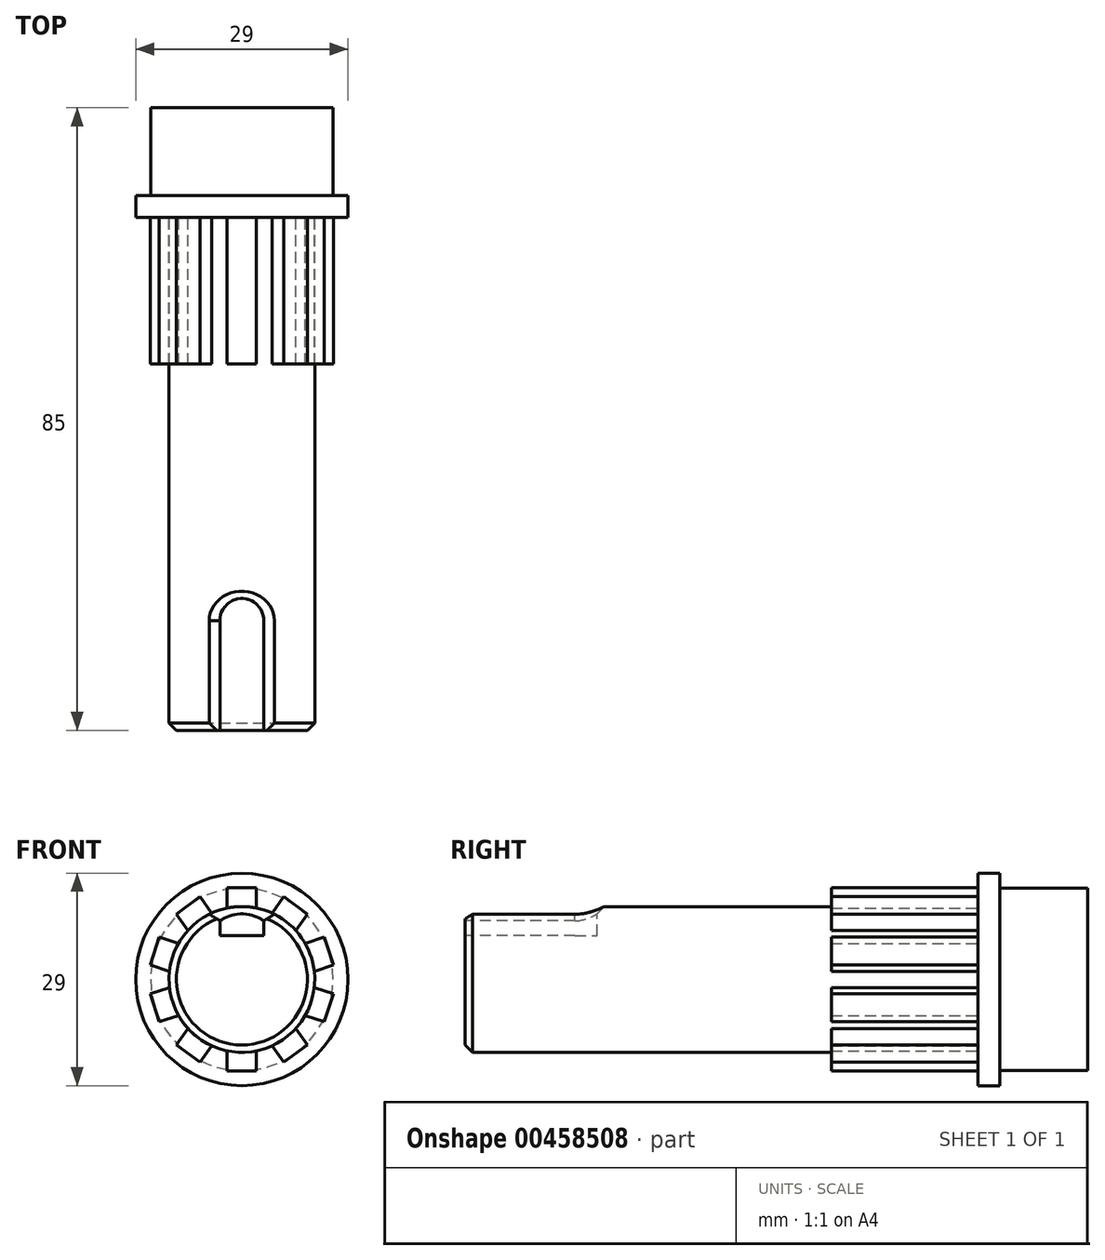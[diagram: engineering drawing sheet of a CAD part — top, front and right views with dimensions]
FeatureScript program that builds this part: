
annotation { "Feature Type Name" : "Feature", "Feature Type Description" : "" }
export const myFeature = defineFeature(function(context is Context, id is Id, definition is map)
    precondition{}
    {
        {
            var Q0;
            Q0=qCreatedBy(makeId("Front.planeOp"),FACE);
            var sketch = newSketch(context, id + "F0", { "sketchPlane" : qUnion([Q0])});
            skCircle(sketch, "E0", {"center": v(0, 0) * mm, "radius": 9.95 * mm});
            skLineSegment(sketch, "E1.bottom", {"start": v(-12.5, 2) * mm, "end": v(12.5, 2) * mm});
            skLineSegment(sketch, "E1.top", {"start": v(-12.5, -2) * mm, "end": v(12.5, -2) * mm});
            skLineSegment(sketch, "E1.left", {"start": v(-12.5, 2) * mm, "end": v(-12.5, -2) * mm});
            skLineSegment(sketch, "E1.right", {"start": v(12.5, 2) * mm, "end": v(12.5, -2) * mm});
            skSolve(sketch);
        }
        {
            var Q0;
            {var subQ0=sQuery(id+"F0.wireOp",EDGE,"E1.bottom");var subQ1=sQuery(id+"F0.wireOp",EDGE,"E0");var subQ2=makeQuery(id+"F0.imprint","INTERSECT",VERTEX,{"disambiguationData":[OD(0.0)],"derivedFrom":[subQ1,subQ0]});Q0=makeQuery(id+"F0.imprint","IMPRINT",FACE,{"disambiguationData":[TD([[makeQuery(id+"F0.imprint","IMPRINT",EDGE,{"disambiguationData":[TD([[subQ2,1.0]])],"derivedFrom":subQ1}),1.0]])]});}
            var Q1;
            {var subQ0=sQuery(id+"F0.wireOp",EDGE,"E1.top");var subQ1=sQuery(id+"F0.wireOp",EDGE,"E0");var subQ2=makeQuery(id+"F0.imprint","INTERSECT",VERTEX,{"disambiguationData":[OD(0.0)],"derivedFrom":[subQ1,subQ0]});Q1=makeQuery(id+"F0.imprint","IMPRINT",FACE,{"disambiguationData":[TD([[makeQuery(id+"F0.imprint","IMPRINT",EDGE,{"disambiguationData":[TD([[subQ2,-1.0]])],"derivedFrom":subQ1}),1.0]])]});}
            var Q2;
            {var subQ5=sQuery(id+"F0.wireOp",EDGE,"E1.right");Q2=makeQuery(id+"F0.imprint","IMPRINT",FACE,{"disambiguationData":[TD([[makeQuery(id+"F0.imprint","IMPRINT",EDGE,{"derivedFrom":subQ5}),-1.0]])]});}
            var Q3;
            {var subQ0=sQuery(id+"F0.wireOp",EDGE,"E1.bottom");var subQ1=sQuery(id+"F0.wireOp",EDGE,"E0");var subQ2=makeQuery(id+"F0.imprint","INTERSECT",VERTEX,{"disambiguationData":[OD(0.0)],"derivedFrom":[subQ1,subQ0]});Q3=makeQuery(id+"F0.imprint","IMPRINT",FACE,{"disambiguationData":[TD([[makeQuery(id+"F0.imprint","IMPRINT",EDGE,{"disambiguationData":[TD([[subQ2,-1.0]])],"derivedFrom":subQ1}),1.0]])]});}
            var Q4;
            {var subQ5=sQuery(id+"F0.wireOp",EDGE,"E1.left");Q4=makeQuery(id+"F0.imprint","IMPRINT",FACE,{"disambiguationData":[TD([[makeQuery(id+"F0.imprint","IMPRINT",EDGE,{"derivedFrom":subQ5}),1.0]])]});}
            extrude(context, id + "F1", {"entities" : qUnion([Q0, Q1, Q2, Q3, Q4]), "depth" : 20 * mm});
        }
        {
            var Q0;
            Q0=makeQuery(id+"F1.opExtrude","SWEPT_BODY",BODY,{"disambiguationData":[OSD([sQuery(id+"F0.wireOp",EDGE,"E0"),sQuery(id+"F0.wireOp",EDGE,"E1.bottom"),sQuery(id+"F0.wireOp",EDGE,"E1.top"),sQuery(id+"F0.wireOp",EDGE,"E1.left"),sQuery(id+"F0.wireOp",EDGE,"E1.right")])]});
            var Q1;
            {var subQ0=sQuery(id+"F0.wireOp",EDGE,"E1.top");var subQ1=sQuery(id+"F0.wireOp",EDGE,"E0");Q1=makeQuery(id+"F1.opExtrude","SWEPT_FACE",FACE,{"disambiguationData":[OSD([subQ1]),TDD([makeQuery(id+"F0.imprint","IMPRINT",EDGE,{"disambiguationData":[TD([[makeQuery(id+"F0.imprint","INTERSECT",VERTEX,{"disambiguationData":[OD(0.0)],"derivedFrom":[subQ1,subQ0]}),-1.0]])],"derivedFrom":subQ1})])]});}
            circularPattern(context, id + "F2", {"operationType" : NewBodyOperationType.ADD, "entities" : qUnion([Q0]), "axis" : qUnion([Q1]), "angle" : 360 * degree, "instanceCount" : 10, "oppositeDirection" : true, "equalSpace" : true});
        }
        {
            var Q0;
            {var subQ0=makeQuery(id+"F1.opExtrude","CAP_FACE",FACE,{"disambiguationData":[OSD([sQuery(id+"F0.wireOp",EDGE,"E0"),sQuery(id+"F0.wireOp",EDGE,"E1.bottom"),sQuery(id+"F0.wireOp",EDGE,"E1.top"),sQuery(id+"F0.wireOp",EDGE,"E1.left"),sQuery(id+"F0.wireOp",EDGE,"E1.right")])],"isStart":false});Q0=makeQuery(id+"F2.boolean.opBoolean","MERGE",FACE,{"derivedFrom":[subQ0,makeQuery(id+"F2.opPattern","COPY",FACE,{"derivedFrom":subQ0,"instanceName":"1"}),makeQuery(id+"F2.opPattern","COPY",FACE,{"derivedFrom":subQ0,"instanceName":"2"}),makeQuery(id+"F2.opPattern","COPY",FACE,{"derivedFrom":subQ0,"instanceName":"3"}),makeQuery(id+"F2.opPattern","COPY",FACE,{"derivedFrom":subQ0,"instanceName":"4"}),makeQuery(id+"F2.opPattern","COPY",FACE,{"derivedFrom":subQ0,"instanceName":"5"}),makeQuery(id+"F2.opPattern","COPY",FACE,{"derivedFrom":subQ0,"instanceName":"6"}),makeQuery(id+"F2.opPattern","COPY",FACE,{"derivedFrom":subQ0,"instanceName":"7"}),makeQuery(id+"F2.opPattern","COPY",FACE,{"derivedFrom":subQ0,"instanceName":"8"}),makeQuery(id+"F2.opPattern","COPY",FACE,{"derivedFrom":subQ0,"instanceName":"9"})]});}
            var sketch = newSketch(context, id + "F3", { "sketchPlane" : qUnion([Q0])});
            skCircle(sketch, "E2", {"center": v(0, 0) * mm, "radius": 9.95 * mm});
            skSolve(sketch);
        }
        {
            var Q0;
            {var subQ0=sQuery(id+"F3.wireOp",EDGE,"E2");var subQ2=sQuery(id+"F0.wireOp",EDGE,"E1.bottom");var subQ9=sQuery(id+"F0.wireOp",EDGE,"E1.right");var subQ10=makeQuery(id+"F1.opExtrude","CAP_EDGE",EDGE,{"disambiguationData":[OSD([subQ2]),TDD([makeQuery(id+"F0.imprint","IMPRINT",EDGE,{"disambiguationData":[TD([[makeQuery(id+"F0.imprint","INTERSECT",VERTEX,{"derivedFrom":[subQ2,subQ9]}),1.0]])],"derivedFrom":subQ2})])],"isStart":false});var subQ17=makeQuery(id+"F3.imprint","INTERSECT",VERTEX,{"derivedFrom":[subQ10,subQ0]});Q0=makeQuery(id+"F3.imprint","IMPRINT",FACE,{"disambiguationData":[TD([[makeQuery(id+"F3.imprint","IMPRINT",EDGE,{"disambiguationData":[TD([[subQ17,-1.0]])],"derivedFrom":subQ0}),1.0]])]});}
            extrude(context, id + "F4", {"entities" : qUnion([Q0]), "operationType" : NewBodyOperationType.ADD, "depth" : 50 * mm});
        }
        {
            var Q0;
            Q0=qCreatedBy(makeId("Front.planeOp"),FACE);
            var sketch = newSketch(context, id + "F5", { "sketchPlane" : qUnion([Q0])});
            skCircle(sketch, "E3", {"center": v(0, 0) * mm, "radius": 14.5 * mm});
            skSolve(sketch);
        }
        {
            var Q0;
            Q0=makeQuery(id+"F5.imprint","IMPRINT",FACE,{"disambiguationData":[TD([[makeQuery(id+"F5.imprint","IMPRINT",EDGE,{"derivedFrom":sQuery(id+"F5.wireOp",EDGE,"E3")}),1.0]])]});
            extrude(context, id + "F6", {"entities" : qUnion([Q0]), "operationType" : NewBodyOperationType.ADD, "oppositeDirection" : true, "depth" : 3 * mm});
        }
        {
            var Q0;
            Q0=makeQuery(id+"F6.opExtrude","CAP_FACE",FACE,{"disambiguationData":[OSD([sQuery(id+"F5.wireOp",EDGE,"E3")])],"isStart":false});
            var sketch = newSketch(context, id + "F7", { "sketchPlane" : qUnion([Q0])});
            skCircle(sketch, "E4", {"center": v(0, 0) * mm, "radius": 12.45 * mm});
            skSolve(sketch);
        }
        {
            var Q0;
            Q0=makeQuery(id+"F7.imprint","IMPRINT",FACE,{"disambiguationData":[TD([[makeQuery(id+"F7.imprint","IMPRINT",EDGE,{"derivedFrom":sQuery(id+"F7.wireOp",EDGE,"E4")}),1.0]])]});
            extrude(context, id + "F8", {"entities" : qUnion([Q0]), "operationType" : NewBodyOperationType.ADD, "depth" : 12 * mm, "offsetDistance" : 25 * mm});
        }
        {
            var Q0;
            Q0=makeQuery(id+"F4.opExtrude","CAP_FACE",FACE,{"disambiguationData":[OSD([sQuery(id+"F3.wireOp",EDGE,"E2")])],"isStart":false});
            var sketch = newSketch(context, id + "F9", { "sketchPlane" : qUnion([Q0])});
            skLineSegment(sketch, "E5", {"start": v(0, 0) * mm, "end": v(-6, 0) * mm, "construction": true});
            skLineSegment(sketch, "E6", {"start": v(-6, 0) * mm, "end": v(-6, 3) * mm});
            skLineSegment(sketch, "E7", {"start": v(-6, 0) * mm, "end": v(-6, -3) * mm});
            skLineSegment(sketch, "E8", {"start": v(-6, -3) * mm, "end": v(-6, 0) * mm});
            skLineSegment(sketch, "E9", {"start": v(-6, -3) * mm, "end": v(-9.49, -3) * mm});
            skLineSegment(sketch, "E10", {"start": v(-6, 3) * mm, "end": v(-9.49, 3) * mm});
            skSolve(sketch);
        }
        {
            var Q0;
            Q0=makeQuery(id+"F9.imprint","IMPRINT",FACE,{"disambiguationData":[TD([[makeQuery(id+"F9.imprint","IMPRINT",EDGE,{"derivedFrom":sQuery(id+"F9.wireOp",EDGE,"E6")}),1.0]])]});
            extrude(context, id + "F10", {"entities" : qUnion([Q0]), "operationType" : NewBodyOperationType.REMOVE, "oppositeDirection" : true, "depth" : 15 * mm});
        }
        {
            var Q0;
            Q0=qCreatedBy(makeId("Right.planeOp"),FACE);
            cPlane(context, id + "F11", {"entities" : qUnion([Q0]), "cplaneType" : CPlaneType.OFFSET, "offset" : 9.95 * mm, "oppositeDirection" : true, "width" : 150 * mm, "height" : 150 * mm});
        }
        {
            var Q0;
            Q0=qCreatedBy(id+"F11.planeOp",FACE);
            var sketch = newSketch(context, id + "F12", { "sketchPlane" : qUnion([Q0])});
            skArc(sketch, "E11", {"start": v(-55, -3) * mm, "mid": v(-52, 0) * mm, "end": v(-55, 3) * mm});
            skLineSegment(sketch, "E12", {"start": v(-55, 3) * mm, "end": v(-55, -3) * mm});
            skSolve(sketch);
        }
        {
            var Q0;
            Q0=makeQuery(id+"F12.imprint","IMPRINT",FACE,{"disambiguationData":[TD([[makeQuery(id+"F12.imprint","IMPRINT",EDGE,{"derivedFrom":sQuery(id+"F12.wireOp",EDGE,"E11")}),1.0]])]});
            extrude(context, id + "F13", {"entities" : qUnion([Q0]), "operationType" : NewBodyOperationType.REMOVE, "depth" : 3.95 * mm});
        }
        {
            var Q0;
            Q0=makeQuery(id+"F4.opExtrude","CAP_EDGE",EDGE,{"disambiguationData":[OSD([sQuery(id+"F3.wireOp",EDGE,"E2")])],"isStart":false});
            chamfer(context, id + "F14", {"entities" : qUnion([Q0]), "width" : 1 * mm, "tangentPropagation" : true});
        }
        {
            var Q0;
            {var subQ0=sQuery(id+"F0.wireOp",EDGE,"E1.left");var subQ1=sQuery(id+"F0.wireOp",EDGE,"E1.top");var subQ2=sQuery(id+"F0.wireOp",EDGE,"E0");var subQ3=makeQuery(id+"F0.imprint","INTERSECT",VERTEX,{"disambiguationData":[OD(0.0)],"derivedFrom":[subQ2,subQ1]});var subQ4=makeQuery(id+"F1.opExtrude","SWEPT_FACE",FACE,{"disambiguationData":[OSD([subQ1]),TDD([makeQuery(id+"F0.imprint","IMPRINT",EDGE,{"disambiguationData":[TD([[makeQuery(id+"F0.imprint","INTERSECT",VERTEX,{"derivedFrom":[subQ1,subQ0]}),-1.0]])],"derivedFrom":subQ1})])]});var subQ5=sQuery(id+"F0.wireOp",EDGE,"E1.right");var subQ6=sQuery(id+"F0.wireOp",EDGE,"E1.bottom");var subQ13=makeQuery(id+"F0.imprint","INTERSECT",VERTEX,{"disambiguationData":[OD(0.0)],"derivedFrom":[subQ2,subQ6]});var subQ14=makeQuery(id+"F1.opExtrude","SWEPT_FACE",FACE,{"disambiguationData":[OSD([subQ6]),TDD([makeQuery(id+"F0.imprint","IMPRINT",EDGE,{"disambiguationData":[TD([[makeQuery(id+"F0.imprint","INTERSECT",VERTEX,{"derivedFrom":[subQ6,subQ0]}),-1.0]])],"derivedFrom":subQ6})])]});var subQ30=makeQuery(id+"F1.opExtrude","SWEPT_FACE",FACE,{"disambiguationData":[OSD([subQ2]),TDD([makeQuery(id+"F0.imprint","IMPRINT",EDGE,{"disambiguationData":[TD([[subQ3,-1.0]])],"derivedFrom":subQ2})])]});var subQ31=makeQuery(id+"F1.opExtrude","SWEPT_FACE",FACE,{"disambiguationData":[OSD([subQ1]),TDD([makeQuery(id+"F0.imprint","IMPRINT",EDGE,{"disambiguationData":[TD([[makeQuery(id+"F0.imprint","INTERSECT",VERTEX,{"derivedFrom":[subQ1,subQ5]}),1.0]])],"derivedFrom":subQ1})])]});var subQ33=makeQuery(id+"F1.opExtrude","SWEPT_FACE",FACE,{"disambiguationData":[OSD([subQ6]),TDD([makeQuery(id+"F0.imprint","IMPRINT",EDGE,{"disambiguationData":[TD([[makeQuery(id+"F0.imprint","INTERSECT",VERTEX,{"derivedFrom":[subQ6,subQ5]}),1.0]])],"derivedFrom":subQ6})])]});var subQ34=makeQuery(id+"F1.opExtrude","SWEPT_FACE",FACE,{"disambiguationData":[OSD([subQ2]),TDD([makeQuery(id+"F0.imprint","IMPRINT",EDGE,{"disambiguationData":[TD([[subQ13,1.0]])],"derivedFrom":subQ2})])]});Q0=makeQuery(id+"F13.boolean.opBoolean","INTERSECT",EDGE,{"derivedFrom":[makeQuery(id+"F4.boolean.opBoolean","MERGE",FACE,{"derivedFrom":[makeQuery(id+"F2.boolean.opBoolean","SPLIT",FACE,{"disambiguationData":[TD([subQ14])],"derivedFrom":subQ34}),makeQuery(id+"F2.boolean.opBoolean","SPLIT",FACE,{"disambiguationData":[TD([subQ33])],"derivedFrom":subQ34}),makeQuery(id+"F2.boolean.opBoolean","SPLIT",FACE,{"disambiguationData":[TD([makeQuery(id+"F2.opPattern","COPY",FACE,{"derivedFrom":subQ33,"instanceName":"1"})])],"derivedFrom":subQ34}),makeQuery(id+"F2.boolean.opBoolean","SPLIT",FACE,{"disambiguationData":[TD([makeQuery(id+"F2.opPattern","COPY",FACE,{"derivedFrom":subQ33,"instanceName":"2"})])],"derivedFrom":subQ34}),makeQuery(id+"F2.boolean.opBoolean","SPLIT",FACE,{"disambiguationData":[TD([makeQuery(id+"F2.opPattern","COPY",FACE,{"derivedFrom":subQ33,"instanceName":"3"})])],"derivedFrom":subQ34}),makeQuery(id+"F2.boolean.opBoolean","SPLIT",FACE,{"disambiguationData":[TD([subQ4])],"derivedFrom":subQ30}),makeQuery(id+"F2.boolean.opBoolean","SPLIT",FACE,{"disambiguationData":[TD([subQ31])],"derivedFrom":subQ30}),makeQuery(id+"F2.boolean.opBoolean","SPLIT",FACE,{"disambiguationData":[TD([makeQuery(id+"F2.opPattern","COPY",FACE,{"derivedFrom":subQ4,"instanceName":"1"})])],"derivedFrom":subQ30}),makeQuery(id+"F2.boolean.opBoolean","SPLIT",FACE,{"disambiguationData":[TD([makeQuery(id+"F2.opPattern","COPY",FACE,{"derivedFrom":subQ4,"instanceName":"2"})])],"derivedFrom":subQ30}),makeQuery(id+"F2.boolean.opBoolean","SPLIT",FACE,{"disambiguationData":[TD([makeQuery(id+"F2.opPattern","COPY",FACE,{"derivedFrom":subQ4,"instanceName":"3"})])],"derivedFrom":subQ30}),makeQuery(id+"F4.opExtrude","SWEPT_FACE",FACE,{"disambiguationData":[OSD([sQuery(id+"F3.wireOp",EDGE,"E2")])]})]}),makeQuery(id+"F13.opExtrude","SWEPT_FACE",FACE,{"disambiguationData":[OSD([sQuery(id+"F12.wireOp",EDGE,"E11")])]})]});}
            chamfer(context, id + "F15", {"entities" : qUnion([Q0]), "width" : 1 * mm, "tangentPropagation" : true});
        }
        {
            var Q0;
            Q0=makeQuery(id+"F1.opExtrude","SWEPT_BODY",BODY,{"disambiguationData":[OSD([sQuery(id+"F0.wireOp",EDGE,"E0"),sQuery(id+"F0.wireOp",EDGE,"E1.bottom"),sQuery(id+"F0.wireOp",EDGE,"E1.top"),sQuery(id+"F0.wireOp",EDGE,"E1.left"),sQuery(id+"F0.wireOp",EDGE,"E1.right")])]});
            var Q1;
            Q1=makeQuery(id+"F14.opChamfer","BLEND_FACE",FACE,{"disambiguationData":[OSD([sQuery(id+"F3.wireOp",EDGE,"E2")])]});
            transform(context, id + "F16", {"entities" : qUnion([Q0]), "transformType" : TransformType.ROTATION, "transformAxis" : qUnion([Q1]), "angle" : 90 * degree, "makeCopy" : false});
        }
    });
